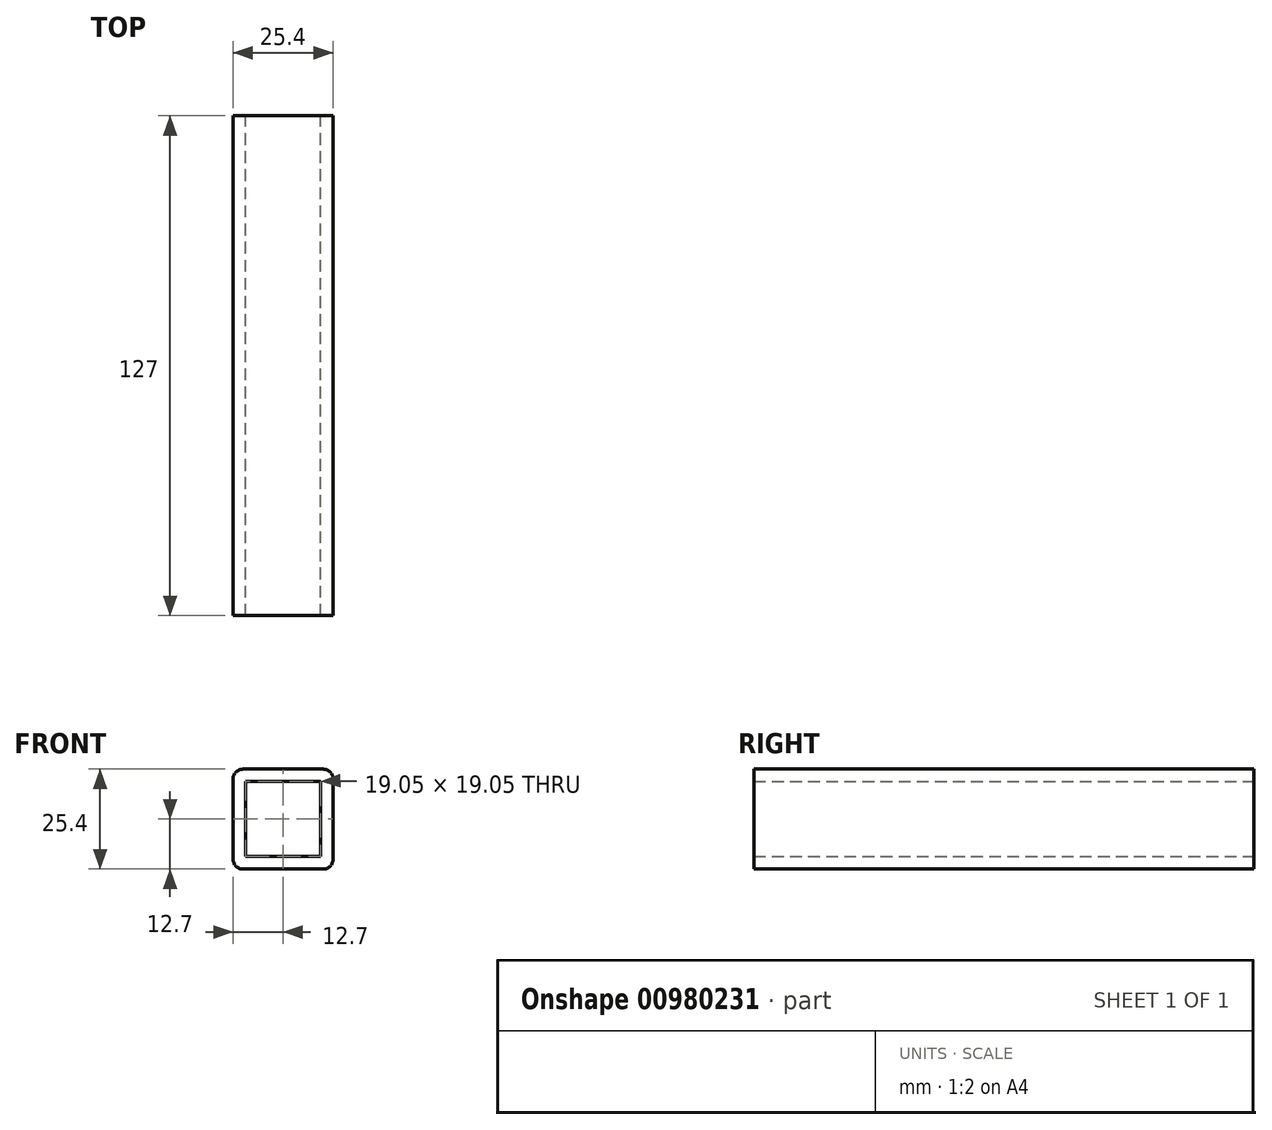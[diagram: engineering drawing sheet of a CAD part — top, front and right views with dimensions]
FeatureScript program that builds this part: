
annotation { "Feature Type Name" : "Feature", "Feature Type Description" : "" }
export const myFeature = defineFeature(function(context is Context, id is Id, definition is map)
    precondition{}
    {
        {
            var Q0;
            Q0=qCreatedBy(makeId("Front.planeOp"),FACE);
            var sketch = newSketch(context, id + "F0", { "sketchPlane" : qUnion([Q0])});
            skLineSegment(sketch, "E0.bottom", {"start": v(12.7, 12.7) * mm, "end": v(-12.7, 12.7) * mm});
            skLineSegment(sketch, "E0.top", {"start": v(12.7, -12.7) * mm, "end": v(-12.7, -12.7) * mm});
            skLineSegment(sketch, "E0.left", {"start": v(12.7, 12.7) * mm, "end": v(12.7, -12.7) * mm});
            skLineSegment(sketch, "E0.right", {"start": v(-12.7, 12.7) * mm, "end": v(-12.7, -12.7) * mm});
            skPoint(sketch, "E0.middle", {"position": v(0, 0) * mm});
            skLineSegment(sketch, "E1.0", {"start": v(9.53, -9.53) * mm, "end": v(-9.53, -9.53) * mm});
            skLineSegment(sketch, "E1.1", {"start": v(9.53, 9.53) * mm, "end": v(9.53, -9.53) * mm});
            skLineSegment(sketch, "E1.2", {"start": v(9.53, 9.53) * mm, "end": v(-9.53, 9.53) * mm});
            skLineSegment(sketch, "E1.3", {"start": v(-9.53, 9.53) * mm, "end": v(-9.53, -9.53) * mm});
            skSolve(sketch);
        }
        {
            var Q0;
            Q0=makeQuery(id+"F0.imprint","IMPRINT",FACE,{"disambiguationData":[TD([[makeQuery(id+"F0.imprint","IMPRINT",EDGE,{"derivedFrom":sQuery(id+"F0.wireOp",EDGE,"E0.bottom")}),1.0]])]});
            extrude(context, id + "F1", {"entities" : qUnion([Q0]), "depth" : 127 * mm, "offsetDistance" : 25.4 * mm});
        }
        {
            var Q0;
            Q0=makeQuery(id+"F1.opExtrude","SWEPT_EDGE",EDGE,{"disambiguationData":[OSD([sQuery(id+"F0.wireOp",EDGE,"E0.top"),sQuery(id+"F0.wireOp",EDGE,"E0.right")])]});
            var Q1;
            Q1=makeQuery(id+"F1.opExtrude","SWEPT_EDGE",EDGE,{"disambiguationData":[OSD([sQuery(id+"F0.wireOp",EDGE,"E0.top"),sQuery(id+"F0.wireOp",EDGE,"E0.left")])]});
            var Q2;
            Q2=makeQuery(id+"F1.opExtrude","SWEPT_EDGE",EDGE,{"disambiguationData":[OSD([sQuery(id+"F0.wireOp",EDGE,"E0.bottom"),sQuery(id+"F0.wireOp",EDGE,"E0.right")])]});
            var Q3;
            Q3=makeQuery(id+"F1.opExtrude","SWEPT_EDGE",EDGE,{"disambiguationData":[OSD([sQuery(id+"F0.wireOp",EDGE,"E0.bottom"),sQuery(id+"F0.wireOp",EDGE,"E0.left")])]});
            fillet(context, id + "F2", {"entities" : qUnion([Q0, Q1, Q2, Q3]), "radius" : 2.54 * mm, "tangentPropagation" : true, "allowEdgeOverflow" : false});
        }
    });
